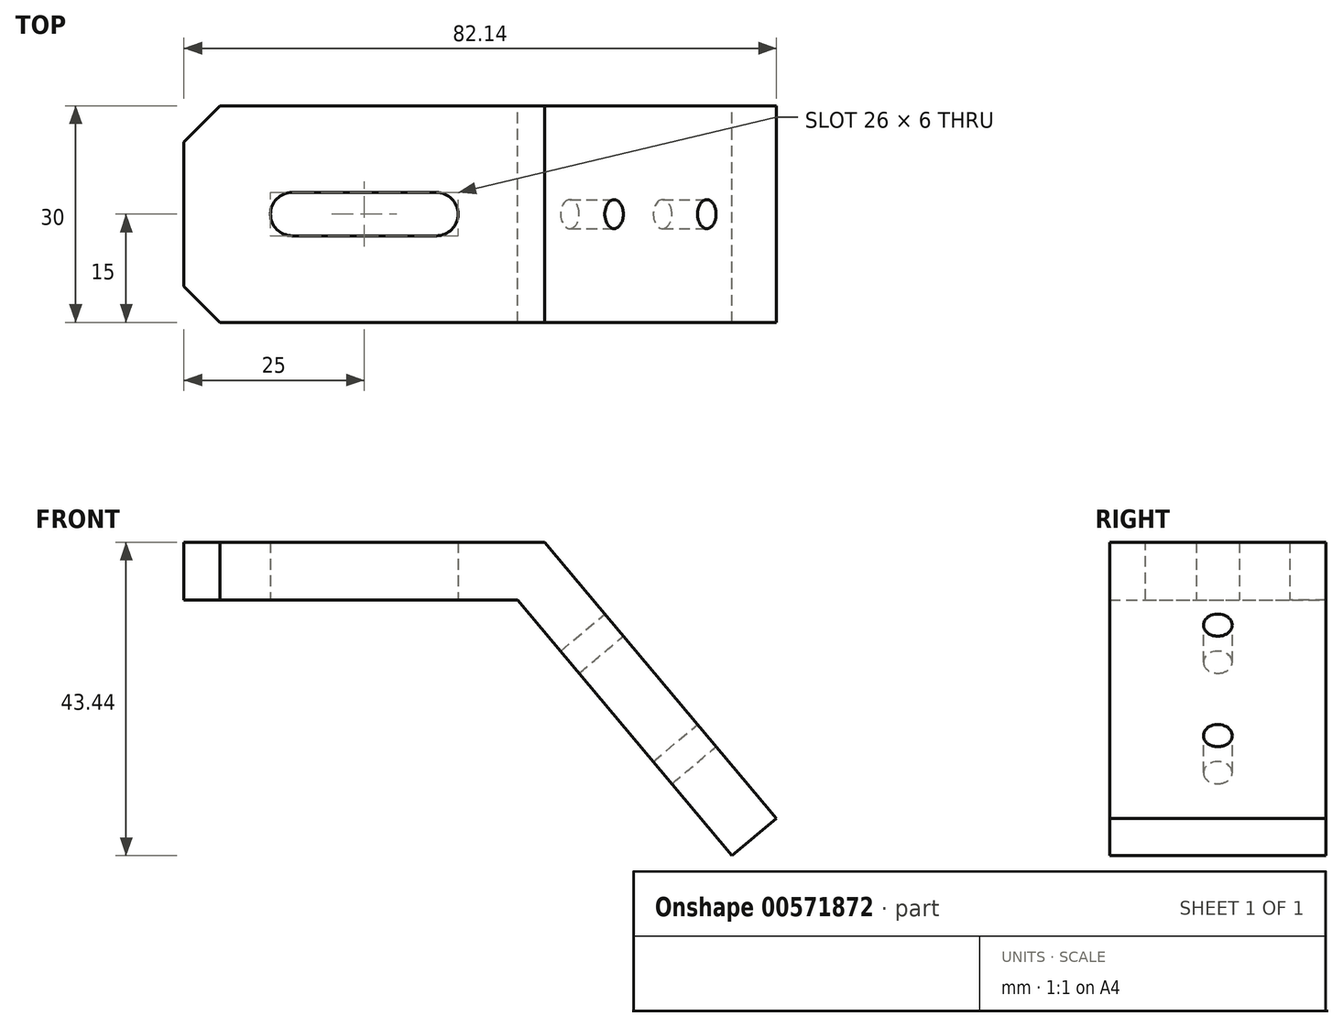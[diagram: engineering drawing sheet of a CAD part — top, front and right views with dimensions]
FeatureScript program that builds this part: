
annotation { "Feature Type Name" : "Feature", "Feature Type Description" : "" }
export const myFeature = defineFeature(function(context is Context, id is Id, definition is map)
    precondition{}
    {
        {
            var Q0;
            Q0=qCreatedBy(makeId("Front.planeOp"),FACE);
            var sketch = newSketch(context, id + "F0", { "sketchPlane" : qUnion([Q0])});
            skLineSegment(sketch, "E0", {"start": v(0, 0) * mm, "end": v(46.27, 0) * mm});
            skLineSegment(sketch, "E1", {"start": v(46.27, 0) * mm, "end": v(76.01, -35.44) * mm});
            skLineSegment(sketch, "E2.0", {"start": v(50, 8) * mm, "end": v(82.14, -30.3) * mm});
            skLineSegment(sketch, "E2.1", {"start": v(0, 8) * mm, "end": v(50, 8) * mm});
            skLineSegment(sketch, "E3", {"start": v(0, 8) * mm, "end": v(0, 0) * mm});
            skLineSegment(sketch, "E4", {"start": v(82.14, -30.3) * mm, "end": v(76.01, -35.44) * mm});
            skSolve(sketch);
        }
        {
            var Q0;
            Q0 = qSketchRegion(id + "F0", true);
            extrude(context, id + "F1", {"entities" : qUnion([Q0]), "endBound" : BoundingType.SYMMETRIC, "depth" : 30 * mm, "offsetDistance" : 25 * mm});
        }
        {
            var Q0;
            Q0=qCreatedBy(makeId("Top.planeOp"),FACE);
            var sketch = newSketch(context, id + "F2", { "sketchPlane" : qUnion([Q0])});
            skLineSegment(sketch, "E5", {"start": v(15, 0) * mm, "end": v(35, 0) * mm});
            skArc(sketch, "E6.0.startCap", {"start": v(15, -3) * mm, "mid": v(12, 0) * mm, "end": v(15, 3) * mm});
            skArc(sketch, "E6.0.endCap", {"start": v(35, 3) * mm, "mid": v(38, 0) * mm, "end": v(35, -3) * mm});
            skLineSegment(sketch, "E6.0.left", {"start": v(15, 3) * mm, "end": v(35, 3) * mm});
            skLineSegment(sketch, "E6.0.right", {"start": v(15, -3) * mm, "end": v(35, -3) * mm});
            skSolve(sketch);
        }
        {
            var Q0;
            Q0 = qSketchRegion(id + "F2", true);
            extrude(context, id + "F3", {"entities" : qUnion([Q0]), "operationType" : NewBodyOperationType.REMOVE, "endBound" : BoundingType.THROUGH_ALL, "depth" : 25 * mm, "offsetDistance" : 25 * mm});
        }
        {
            var Q0;
            Q0=makeQuery(id+"F1.opExtrude","SWEPT_FACE",FACE,{"disambiguationData":[OSD([sQuery(id+"F0.wireOp",EDGE,"E2.0")])]});
            var sketch = newSketch(context, id + "F4", { "sketchPlane" : qUnion([Q0])});
            skPoint(sketch, "E7", {"position": v(0, -41.01) * mm});
            skPoint(sketch, "E8", {"position": v(0, -61.01) * mm});
            skSolve(sketch);
        }
        {
            var Q0;
            Q0=sQuery(id+"F4.wireOp",VERTEX,"E8");
            var Q1;
            Q1=sQuery(id+"F4.wireOp",VERTEX,"E7");
            var Q2;
            Q2=makeQuery(id+"F1.opExtrude","SWEPT_BODY",BODY,{"disambiguationData":[OSD([sQuery(id+"F0.wireOp",EDGE,"E0"),sQuery(id+"F0.wireOp",EDGE,"E1"),sQuery(id+"F0.wireOp",EDGE,"E2.0"),sQuery(id+"F0.wireOp",EDGE,"E2.1"),sQuery(id+"F0.wireOp",EDGE,"E3"),sQuery(id+"F0.wireOp",EDGE,"E4")])]});
            hole(context, id + "F5", {"style" : HoleStyle.SIMPLE, "endStyle" : HoleEndStyle.THROUGH, "holeDiameter" : 4 * mm, "isTappedThrough" : true, "tappedDepth" : 12 * mm, "tapClearance" : 3, "locations" : qUnion([Q0, Q1]), "scope" : qUnion([Q2])});
        }
        {
            var Q0;
            Q0=makeQuery(id+"F1.opExtrude","CAP_EDGE",EDGE,{"disambiguationData":[OSD([sQuery(id+"F0.wireOp",EDGE,"E3")])],"isStart":true});
            var Q1;
            Q1=makeQuery(id+"F1.opExtrude","CAP_EDGE",EDGE,{"disambiguationData":[OSD([sQuery(id+"F0.wireOp",EDGE,"E3")])],"isStart":false});
            chamfer(context, id + "F6", {"entities" : qUnion([Q0, Q1]), "width" : 5 * mm, "tangentPropagation" : true});
        }
    });
